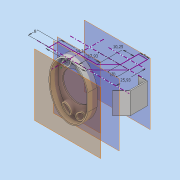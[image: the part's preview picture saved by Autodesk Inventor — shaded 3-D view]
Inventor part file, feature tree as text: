
AUTODESK INVENTOR PART (.ipt)
format: ipt  version: 2019 (Build 230136000, 136)  size: 238,592 bytes
history: native  units: mm
features: other x7, extrude x4, shell x3, sketch x3
ambient origin geometry x8: Origin, YZ Plane, XZ Plane, XY Plane, X Axis, Y Axis, Z Axis, Center Point
bodies: Body1 (feature_tree), Body2 (feature_tree), Body3 (feature_tree)
feature tree (17):
  other  "Твердое тело1"
  extrude  "Выдавливание1"  Depth=34.31mm
  other  "РабПлоскость4"
  extrude  "Круг"  Depth=8.0mm
  shell  "сам корпус"  Thickness=34.31mm
  shell  "Для круга"  Thickness=8.0mm
  other  "РабПлоскость8"
  extrude  "Выдавливание4"  Depth=17.93mm
  other  "РабПлоскость11"
  other  "Дыры в корпусе"
  extrude  "Выдавливание5"  Depth=25.93mm
  shell  "Оболочка5"  Thickness=10.25mm
  sketch  "Эскиз1"
  sketch  "Эскиз7"
  other  "Элипс"
  sketch  "Эскиз12"
  other  "Твердое тело4"
